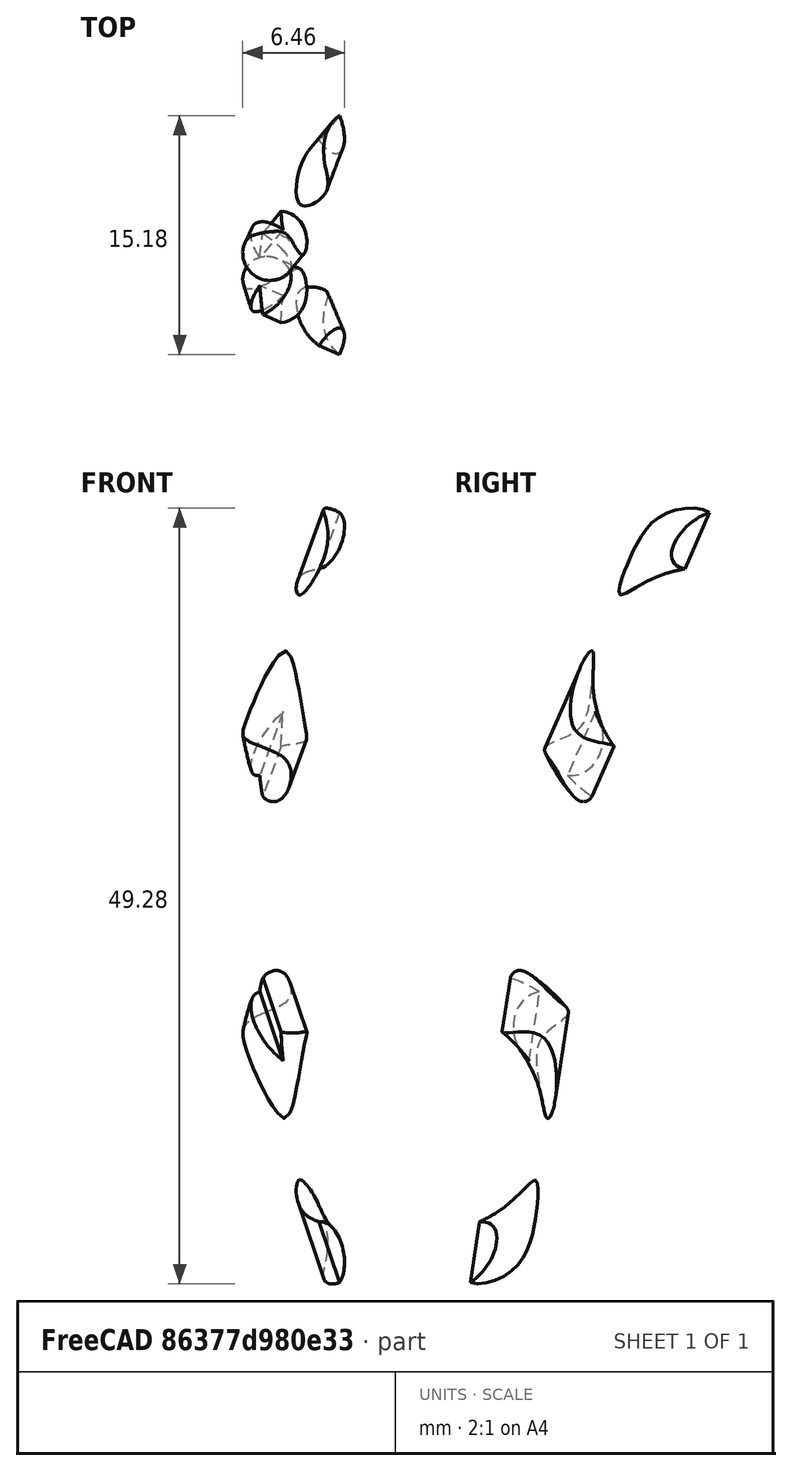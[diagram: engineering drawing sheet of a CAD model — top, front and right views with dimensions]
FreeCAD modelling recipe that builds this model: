
FCSTD DOCUMENT  (FreeCAD 0.18R4 (GitTag))
Label: 3d model
License: All rights reserved
LicenseURL: http://en.wikipedia.org/wiki/All_rights_reserved
objects: Part::MultiCommon×3, Part::Torus×2, Part::Cylinder×2, PartDesign::Body×2, Sketcher::SketchObject×1
note: 10 computed .brp shape members not serialized (recipe doc carries the construction recipe); baked Part::Feature solids carry a one-line shape summary decoded from their .brp

FEATURE [Part::Torus] Torus  label="Тор"
  Angle1 = -180
  Angle2 = 180
  Angle3 = 360
  AttacherType = Attacher::AttachEngine3D
  Placement = pos=(2.29423,-6,-15.0263) rot=(0.686113,0.10177,0.720342;3.46487rad)
  Radius1 = 8.9
  Radius2 = 2
FEATURE [Part::Cylinder] Cylinder  label="Цилиндр"
  Angle = 312
  AttacherType = Attacher::AttachEngine3D
  Height = 37
  Placement = pos=(5.07995,-2.90915,-26.4384) rot=(0.071103,-0.26536,-0.961524;1.39806rad)
  Radius = 2
FEATURE [Part::MultiCommon] Common
  Placement = pos=(0,0,0) rot=(1,0,0;2.87979rad)
  Shapes = -> [Cylinder,Torus]
FEATURE [Part::Torus] Torus001  label="Тор001"
  Angle1 = -180
  Angle2 = 180
  Angle3 = 360
  AttacherType = Attacher::AttachEngine3D
  Placement = pos=(2.29423,-6,-15.0263) rot=(0.686113,0.10177,0.720342;3.46487rad)
  Radius1 = 8.9
  Radius2 = 2
FEATURE [Part::Cylinder] Cylinder001  label="Цилиндр001"
  Angle = 312
  AttacherType = Attacher::AttachEngine3D
  Height = 37
  Placement = pos=(5.07995,-2.90915,-26.4384) rot=(0.071103,-0.26536,-0.961524;1.39806rad)
  Radius = 2
FEATURE [Part::MultiCommon] Common001
  Shapes = -> [Cylinder001,Torus001]
FEATURE [Part::MultiCommon] Common002
  Shapes = -> [Cylinder,Torus]
FEATURE [Sketcher::SketchObject] Sketch
  MapMode = 5
  Placement = pos=(0,0,0) rot=(1,0,0;1.5708rad)
  Support = -> [XZ_Plane]
  sketch-geometry (5):
    g0: LineSegment StartX=-143.728 StartY=52.9453 StartZ=0 EndX=-118.105 EndY=87.6502 EndZ=0
    g1: LineSegment StartX=-118.105 StartY=87.6502 StartZ=0 EndX=-94.4277 EndY=48.0802 EndZ=0
    g2: LineSegment StartX=-94.4277 StartY=48.0802 StartZ=0 EndX=-61.3446 EndY=86.3528 EndZ=0
    g3: LineSegment StartX=-61.3446 StartY=86.3528 StartZ=0 EndX=-51.6143 EndY=51.6479 EndZ=0
    g4: LineSegment StartX=-51.6143 StartY=51.6479 StartZ=0 EndX=-28.5858 EndY=79.5416 EndZ=0
  constraints (4):
    c: Coincident(g0,g1)
    c: Coincident(g1,g2)
    c: Coincident(g2,g3)
    c: Coincident(g3,g4)
FEATURE [PartDesign::Body] Body
  Group = -> [Sketch]
  Origin = -> Origin
FEATURE [PartDesign::Body] Body001
  Origin = -> Origin001
